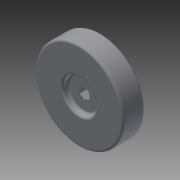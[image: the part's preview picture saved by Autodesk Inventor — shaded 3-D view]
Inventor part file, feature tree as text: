
AUTODESK INVENTOR PART (.ipt)
format: ipt  version: 2015 (Build 190159000, 159)  size: 131,584 bytes
history: native  units: in
note: dims shown in document units (in); Inventor stores cm internally (conversion verified against a paired STEP export)
features: extrude x3, sketch x3, fillet x1
ambient origin geometry x8: Origin, YZ Plane, XZ Plane, XY Plane, X Axis, Y Axis, Z Axis, Center Point
bodies: Solid1 (feature_tree)
feature tree (7):
  extrude  "Extrusion1"  Depth=0.5in TaperAngle=0.0deg
  extrude  "Extrusion2"  Depth=0.5in TaperAngle=0.0deg
  extrude  "Extrusion3"  Depth=0.125in TaperAngle=0.0deg
  fillet  "Fillet3"  Radius=0.05in
  sketch  "Sketch1"  dims[d0=2.0in d1=0.5in d2=0.0in]
  sketch  "Sketch2"  dims[d3=0.1254in d4=0.5in d5=0.0in]
  sketch  "Sketch3"  dims[d6=0.75in d7=0.125in d8=0.0in d11=0.05in]
